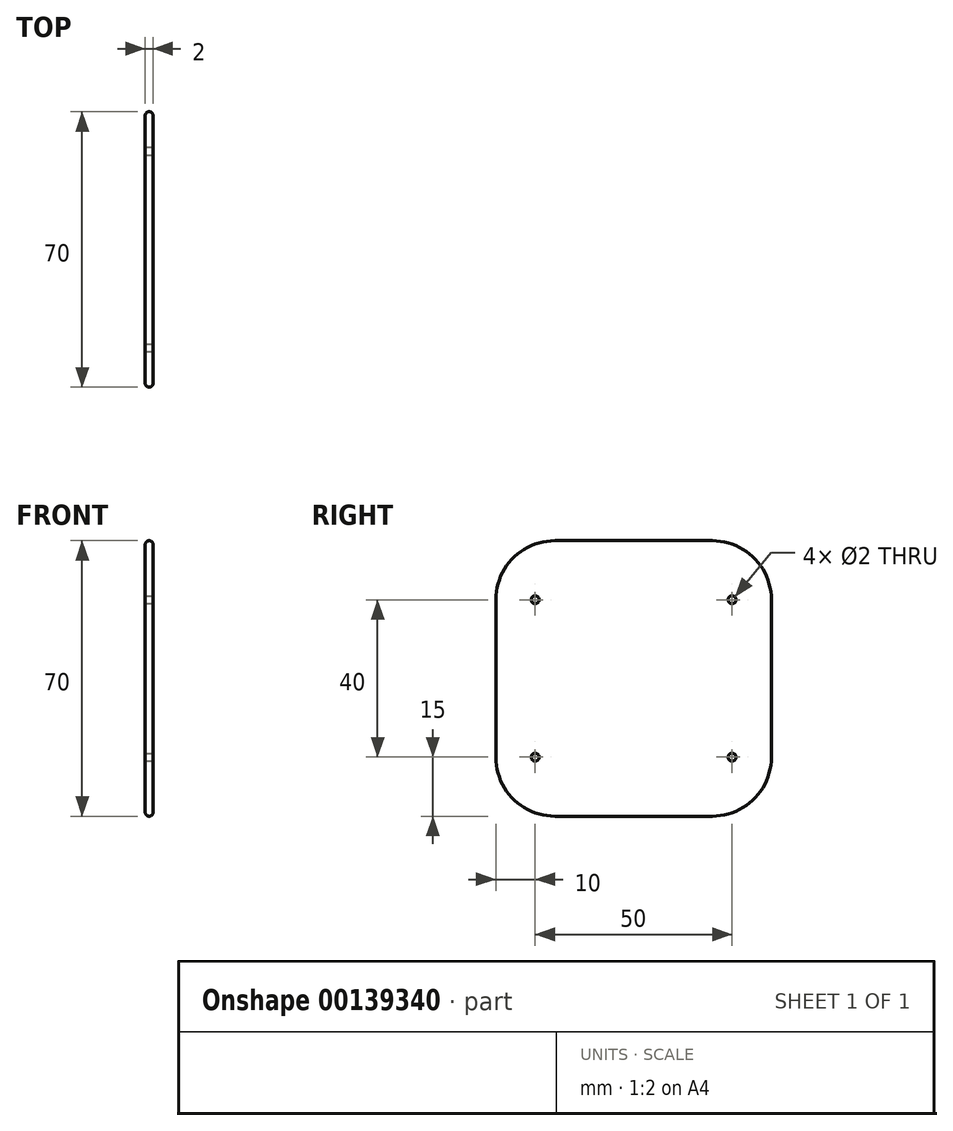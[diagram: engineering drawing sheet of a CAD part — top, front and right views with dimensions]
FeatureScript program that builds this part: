
annotation { "Feature Type Name" : "Feature", "Feature Type Description" : "" }
export const myFeature = defineFeature(function(context is Context, id is Id, definition is map)
    precondition{}
    {
        {
            var Q0;
            Q0=qCreatedBy(makeId("Right.planeOp"),FACE);
            var sketch = newSketch(context, id + "F0", { "sketchPlane" : qUnion([Q0])});
            skLineSegment(sketch, "E0.bottom", {"start": v(20, -35) * mm, "end": v(-20, -35) * mm});
            skLineSegment(sketch, "E0.top", {"start": v(20, 35) * mm, "end": v(-20, 35) * mm});
            skLineSegment(sketch, "E0.left", {"start": v(35, -20) * mm, "end": v(35, 20) * mm});
            skLineSegment(sketch, "E0.right", {"start": v(-35, -20) * mm, "end": v(-35, 20) * mm});
            skPoint(sketch, "E0.middle", {"position": v(0, 0) * mm});
            skPoint(sketch, "E1.visualSharp", {"position": v(-35, 35) * mm});
            skArc(sketch, "E1.filletArc", {"start": v(-20, 35) * mm, "mid": v(-30.6, 30.6) * mm, "end": v(-35, 20) * mm});
            skArc(sketch, "E2.MirrorCS", {"start": v(-20, -35) * mm, "mid": v(-30.6, -30.6) * mm, "end": v(-35, -20) * mm});
            skArc(sketch, "E3.MirrorCS", {"start": v(20, 35) * mm, "mid": v(30.6, 30.6) * mm, "end": v(35, 20) * mm});
            skArc(sketch, "E4.MirrorCS", {"start": v(20, -35) * mm, "mid": v(30.6, -30.6) * mm, "end": v(35, -20) * mm});
            skPoint(sketch, "E5.orphan", {"position": v(-35, -35) * mm});
            skPoint(sketch, "E6.orphan", {"position": v(35, -35) * mm});
            skPoint(sketch, "E7.orphan", {"position": v(35, 35) * mm});
            skSolve(sketch);
        }
        {
            var Q0;
            Q0 = qSketchRegion(id + "F0", true);
            extrude(context, id + "F1", {"entities" : qUnion([Q0]), "depth" : 2 * mm});
        }
        {
            var Q0;
            Q0=makeQuery(id+"F1.opExtrude","CAP_FACE",FACE,{"disambiguationData":[OSD([sQuery(id+"F0.wireOp",EDGE,"E0.bottom"),sQuery(id+"F0.wireOp",EDGE,"E0.top"),sQuery(id+"F0.wireOp",EDGE,"E0.left"),sQuery(id+"F0.wireOp",EDGE,"E0.right"),sQuery(id+"F0.wireOp",EDGE,"E1.filletArc"),sQuery(id+"F0.wireOp",EDGE,"E2.MirrorCS"),sQuery(id+"F0.wireOp",EDGE,"E3.MirrorCS"),sQuery(id+"F0.wireOp",EDGE,"E4.MirrorCS")])],"isStart":true});
            fillet(context, id + "F2", {"entities" : qUnion([Q0]), "radius" : 1 * mm, "tangentPropagation" : true, "allowEdgeOverflow" : false});
        }
        {
            var Q0;
            Q0=makeQuery(id+"F1.opExtrude","CAP_FACE",FACE,{"disambiguationData":[OSD([sQuery(id+"F0.wireOp",EDGE,"E0.bottom"),sQuery(id+"F0.wireOp",EDGE,"E0.top"),sQuery(id+"F0.wireOp",EDGE,"E0.left"),sQuery(id+"F0.wireOp",EDGE,"E0.right"),sQuery(id+"F0.wireOp",EDGE,"E1.filletArc"),sQuery(id+"F0.wireOp",EDGE,"E2.MirrorCS"),sQuery(id+"F0.wireOp",EDGE,"E3.MirrorCS"),sQuery(id+"F0.wireOp",EDGE,"E4.MirrorCS")])],"isStart":false});
            fillet(context, id + "F3", {"entities" : qUnion([Q0]), "radius" : 1 * mm, "tangentPropagation" : true, "allowEdgeOverflow" : false});
        }
        {
            var Q0;
            Q0=makeQuery(id+"F1.opExtrude","CAP_FACE",FACE,{"disambiguationData":[OSD([sQuery(id+"F0.wireOp",EDGE,"E0.bottom"),sQuery(id+"F0.wireOp",EDGE,"E0.top"),sQuery(id+"F0.wireOp",EDGE,"E0.left"),sQuery(id+"F0.wireOp",EDGE,"E0.right"),sQuery(id+"F0.wireOp",EDGE,"E1.filletArc"),sQuery(id+"F0.wireOp",EDGE,"E2.MirrorCS"),sQuery(id+"F0.wireOp",EDGE,"E3.MirrorCS"),sQuery(id+"F0.wireOp",EDGE,"E4.MirrorCS")])],"isStart":false});
            var sketch = newSketch(context, id + "F4", { "sketchPlane" : qUnion([Q0])});
            skCircle(sketch, "E8", {"center": v(-25, 20) * mm, "radius": 1 * mm});
            skCircle(sketch, "E9.MirrorC", {"center": v(25, 20) * mm, "radius": 1 * mm});
            skCircle(sketch, "E10.MirrorC", {"center": v(-25, -20) * mm, "radius": 1 * mm});
            skCircle(sketch, "E11.MirrorC", {"center": v(25, -20) * mm, "radius": 1 * mm});
            skSolve(sketch);
        }
        {
            var Q0;
            Q0 = qSketchRegion(id + "F4", true);
            extrude(context, id + "F5", {"entities" : qUnion([Q0]), "operationType" : NewBodyOperationType.REMOVE, "oppositeDirection" : true, "depth" : 2 * mm});
        }
    });
